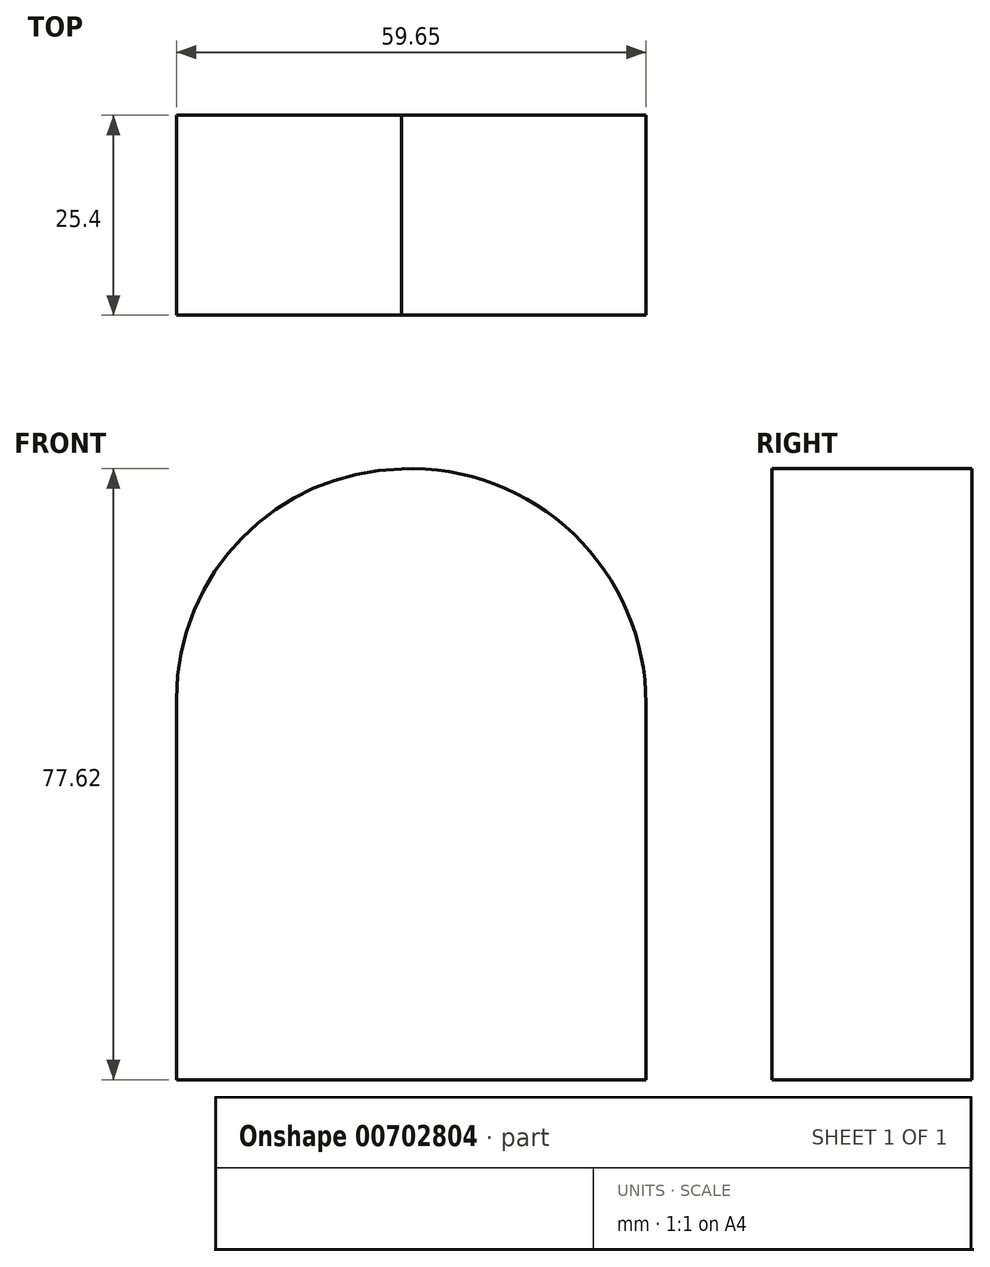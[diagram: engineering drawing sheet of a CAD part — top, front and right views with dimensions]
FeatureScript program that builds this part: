
annotation { "Feature Type Name" : "Feature", "Feature Type Description" : "" }
export const myFeature = defineFeature(function(context is Context, id is Id, definition is map)
    precondition{}
    {
        {
            var Q0;
            Q0=qCreatedBy(makeId("Front.planeOp"),FACE);
            var sketch = newSketch(context, id + "F0", { "sketchPlane" : qUnion([Q0])});
            skLineSegment(sketch, "E0", {"start": v(-76.28, 8.36) * mm, "end": v(-76.28, -40) * mm});
            skLineSegment(sketch, "E1", {"start": v(-76.28, -40) * mm, "end": v(-16.63, -40) * mm});
            skLineSegment(sketch, "E2", {"start": v(-16.63, -40) * mm, "end": v(-16.63, 7.76) * mm});
            skLineSegment(sketch, "E3", {"start": v(-16.63, 7.76) * mm, "end": v(-76.28, 7.76) * mm});
            skArc(sketch, "E4", {"start": v(-47.66, 37.59) * mm, "mid": v(-67.94, 28.81) * mm, "end": v(-76.28, 8.36) * mm});
            skArc(sketch, "E5", {"start": v(-16.63, 7.76) * mm, "mid": v(-25.8, 29.28) * mm, "end": v(-47.66, 37.59) * mm});
            skSolve(sketch);
        }
        {
            var Q0;
            {var subQ0=sQuery(id+"F0.wireOp",EDGE,"E1");Q0=makeQuery(id+"F0.imprint","IMPRINT",FACE,{"disambiguationData":[TD([[makeQuery(id+"F0.imprint","IMPRINT",EDGE,{"derivedFrom":subQ0}),1.0]])]});}
            var Q1;
            {var subQ2=sQuery(id+"F0.wireOp",EDGE,"E3");Q1=makeQuery(id+"F0.imprint","IMPRINT",FACE,{"disambiguationData":[TD([[makeQuery(id+"F0.imprint","IMPRINT",EDGE,{"derivedFrom":subQ2}),-1.0]])]});}
            extrude(context, id + "F1", {"entities" : qUnion([Q0, Q1]), "depth" : 25.4 * mm, "offsetDistance" : 25.4 * mm});
        }
    });
